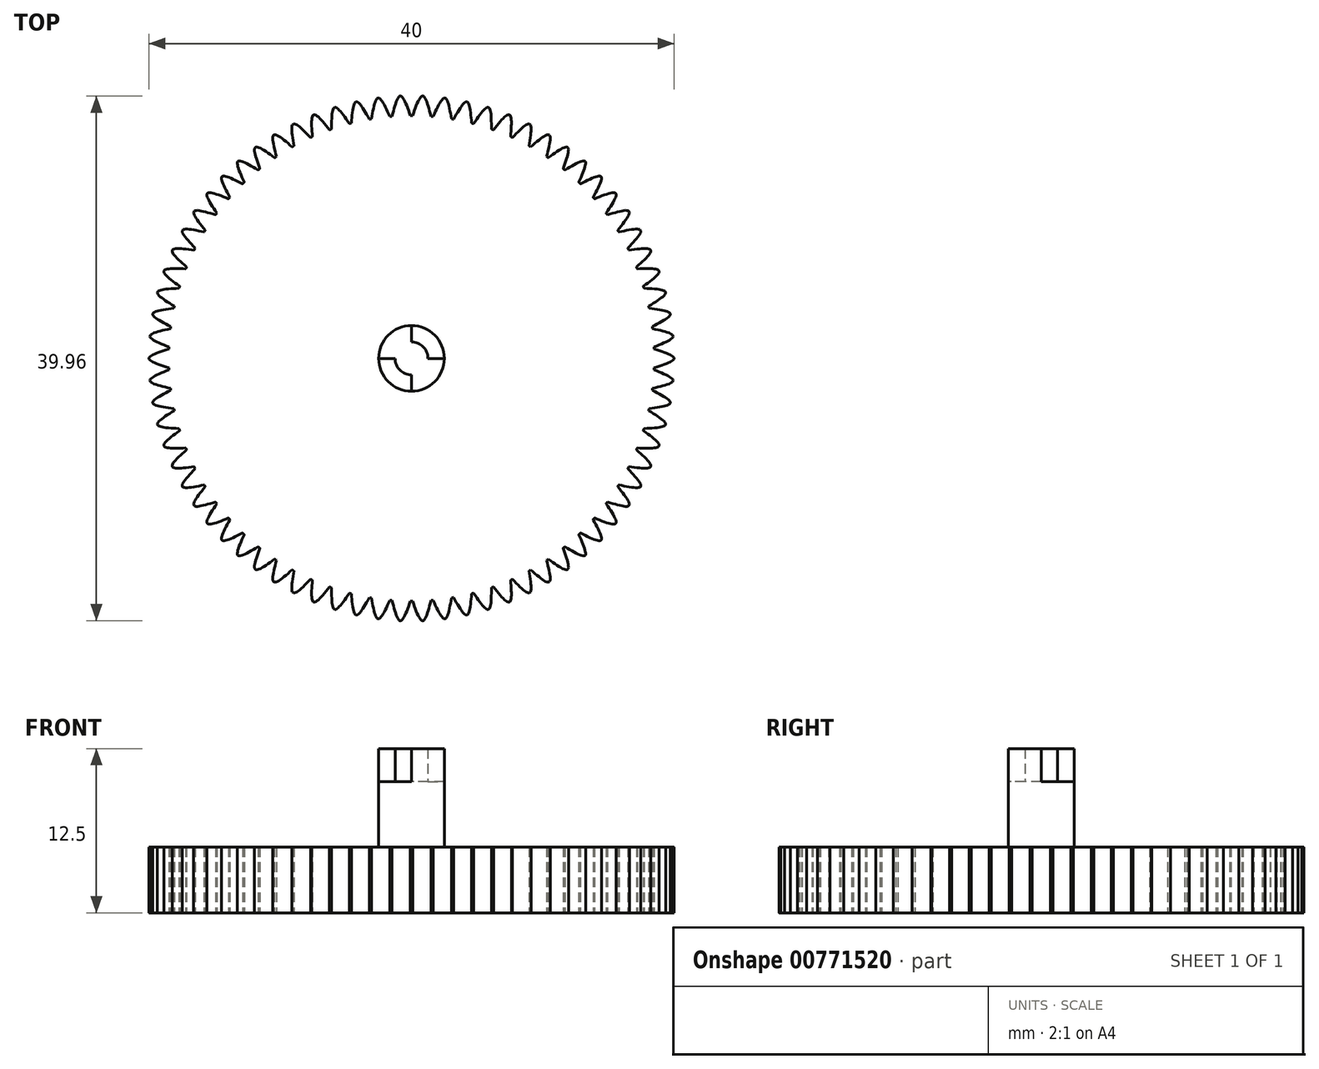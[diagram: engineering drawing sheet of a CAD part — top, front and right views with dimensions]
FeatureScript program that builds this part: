
annotation { "Feature Type Name" : "Feature", "Feature Type Description" : "" }
export const myFeature = defineFeature(function(context is Context, id is Id, definition is map)
    precondition{}
    {
        {
            var Q0;
            Q0=qCreatedBy(makeId("Top.planeOp"),FACE);
            var sketch = newSketch(context, id + "F0", { "sketchPlane" : qUnion([Q0])});
            skLineSegment(sketch, "E0", {"start": v(0, 0) * mm, "end": v(18.5, 0) * mm, "construction": true});
            skLineSegment(sketch, "E1", {"start": v(18.5, 0) * mm, "end": v(-20, 0) * mm, "construction": true});
            skCircle(sketch, "E2", {"center": v(0, 0) * mm, "radius": 18.5 * mm});
            skLineSegment(sketch, "E3", {"start": v(-18.5, 0) * mm, "end": v(-18.5, 0.7) * mm, "construction": true});
            skLineSegment(sketch, "E4", {"start": v(-18.5, 0.7) * mm, "end": v(-18.5, -0.7) * mm, "construction": true});
            skLineSegment(sketch, "E5", {"start": v(-18.5, -0.7) * mm, "end": v(-18.49, -0.7) * mm, "construction": true});
            skLineSegment(sketch, "E6", {"start": v(-18.49, -0.7) * mm, "end": v(-18.49, 0.7) * mm, "construction": true});
            skLineSegment(sketch, "E7", {"start": v(-18.49, 0.7) * mm, "end": v(-18.5, 0.7) * mm, "construction": true});
            skFitSpline(sketch, "E8", {"points": [v(-18.49, -0.7) * mm, v(-20, 0) * mm, v(-18.49, 0.7) * mm], "startDerivative": vector(-4.69, 1.4) * mm, "endDerivative": vector(4.69, 1.4) * mm});
            skSolve(sketch);
        }
        {
            var Q0;
            {var subQ0=sQuery(id+"F0.wireOp",EDGE,"E8");var subQ1=sQuery(id+"F0.wireOp",EDGE,"E2");var subQ2=makeQuery(id+"F0.imprint","INTERSECT",VERTEX,{"disambiguationData":[OD(0.0)],"derivedFrom":[subQ1,subQ0]});Q0=makeQuery(id+"F0.imprint","IMPRINT",FACE,{"disambiguationData":[TD([[makeQuery(id+"F0.imprint","IMPRINT",EDGE,{"disambiguationData":[TD([[subQ2,1.0]])],"derivedFrom":subQ1}),1.0]])]});}
            var Q1;
            {var subQ0=sQuery(id+"F0.wireOp",EDGE,"E8");Q1=makeQuery(id+"F0.imprint","IMPRINT",FACE,{"disambiguationData":[TD([[makeQuery(id+"F0.imprint","IMPRINT",EDGE,{"derivedFrom":subQ0}),-1.0]])]});}
            extrude(context, id + "F1", {"entities" : qUnion([Q0, Q1]), "depth" : 5 * mm, "offsetDistance" : 25 * mm});
        }
        {
            var Q0;
            Q0=makeQuery(id+"F1.opExtrude","SWEPT_BODY",BODY,{"disambiguationData":[OSD([sQuery(id+"F0.wireOp",EDGE,"E2"),sQuery(id+"F0.wireOp",EDGE,"E8")])]});
            var Q1;
            Q1=sQuery(id+"F0.wireOp",EDGE,"E2");
            circularPattern(context, id + "F2", {"entities" : qUnion([Q0]), "axis" : qUnion([Q1]), "angle" : 360 * degree, "instanceCount" : 74, "equalSpace" : true});
        }
        {
            var Q0;
            Q0=makeQuery(id+"F2.opPattern","COPY",BODY,{"derivedFrom":makeQuery(id+"F1.opExtrude","SWEPT_BODY",BODY,{"disambiguationData":[OSD([sQuery(id+"F0.wireOp",EDGE,"rMVjyNJe-mwVF-HOql-274t-2KQgdZwxYzZl"),sQuery(id+"F0.wireOp",EDGE,"E2"),sQuery(id+"F0.wireOp",EDGE,"E8")])]}),"instanceName":"10"});
            var Q1;
            Q1=makeQuery(id+"F2.opPattern","COPY",BODY,{"derivedFrom":makeQuery(id+"F1.opExtrude","SWEPT_BODY",BODY,{"disambiguationData":[OSD([sQuery(id+"F0.wireOp",EDGE,"rMVjyNJe-mwVF-HOql-274t-2KQgdZwxYzZl"),sQuery(id+"F0.wireOp",EDGE,"E2"),sQuery(id+"F0.wireOp",EDGE,"E8")])]}),"instanceName":"16"});
            var Q2;
            Q2=makeQuery(id+"F2.opPattern","COPY",BODY,{"derivedFrom":makeQuery(id+"F1.opExtrude","SWEPT_BODY",BODY,{"disambiguationData":[OSD([sQuery(id+"F0.wireOp",EDGE,"rMVjyNJe-mwVF-HOql-274t-2KQgdZwxYzZl"),sQuery(id+"F0.wireOp",EDGE,"E2"),sQuery(id+"F0.wireOp",EDGE,"E8")])]}),"instanceName":"15"});
            var Q3;
            Q3=makeQuery(id+"F2.opPattern","COPY",BODY,{"derivedFrom":makeQuery(id+"F1.opExtrude","SWEPT_BODY",BODY,{"disambiguationData":[OSD([sQuery(id+"F0.wireOp",EDGE,"rMVjyNJe-mwVF-HOql-274t-2KQgdZwxYzZl"),sQuery(id+"F0.wireOp",EDGE,"E2"),sQuery(id+"F0.wireOp",EDGE,"E8")])]}),"instanceName":"14"});
            var Q4;
            Q4=makeQuery(id+"F2.opPattern","COPY",BODY,{"derivedFrom":makeQuery(id+"F1.opExtrude","SWEPT_BODY",BODY,{"disambiguationData":[OSD([sQuery(id+"F0.wireOp",EDGE,"rMVjyNJe-mwVF-HOql-274t-2KQgdZwxYzZl"),sQuery(id+"F0.wireOp",EDGE,"E2"),sQuery(id+"F0.wireOp",EDGE,"E8")])]}),"instanceName":"13"});
            var Q5;
            Q5=makeQuery(id+"F2.opPattern","COPY",BODY,{"derivedFrom":makeQuery(id+"F1.opExtrude","SWEPT_BODY",BODY,{"disambiguationData":[OSD([sQuery(id+"F0.wireOp",EDGE,"rMVjyNJe-mwVF-HOql-274t-2KQgdZwxYzZl"),sQuery(id+"F0.wireOp",EDGE,"E2"),sQuery(id+"F0.wireOp",EDGE,"E8")])]}),"instanceName":"12"});
            var Q6;
            Q6=makeQuery(id+"F2.opPattern","COPY",BODY,{"derivedFrom":makeQuery(id+"F1.opExtrude","SWEPT_BODY",BODY,{"disambiguationData":[OSD([sQuery(id+"F0.wireOp",EDGE,"rMVjyNJe-mwVF-HOql-274t-2KQgdZwxYzZl"),sQuery(id+"F0.wireOp",EDGE,"E2"),sQuery(id+"F0.wireOp",EDGE,"E8")])]}),"instanceName":"11"});
            var Q7;
            Q7=makeQuery(id+"F2.opPattern","COPY",BODY,{"derivedFrom":makeQuery(id+"F1.opExtrude","SWEPT_BODY",BODY,{"disambiguationData":[OSD([sQuery(id+"F0.wireOp",EDGE,"rMVjyNJe-mwVF-HOql-274t-2KQgdZwxYzZl"),sQuery(id+"F0.wireOp",EDGE,"E2"),sQuery(id+"F0.wireOp",EDGE,"E8")])]}),"instanceName":"9"});
            var Q8;
            Q8=makeQuery(id+"F2.opPattern","COPY",BODY,{"derivedFrom":makeQuery(id+"F1.opExtrude","SWEPT_BODY",BODY,{"disambiguationData":[OSD([sQuery(id+"F0.wireOp",EDGE,"rMVjyNJe-mwVF-HOql-274t-2KQgdZwxYzZl"),sQuery(id+"F0.wireOp",EDGE,"E2"),sQuery(id+"F0.wireOp",EDGE,"E8")])]}),"instanceName":"7"});
            var Q9;
            Q9=makeQuery(id+"F2.opPattern","COPY",BODY,{"derivedFrom":makeQuery(id+"F1.opExtrude","SWEPT_BODY",BODY,{"disambiguationData":[OSD([sQuery(id+"F0.wireOp",EDGE,"rMVjyNJe-mwVF-HOql-274t-2KQgdZwxYzZl"),sQuery(id+"F0.wireOp",EDGE,"E2"),sQuery(id+"F0.wireOp",EDGE,"E8")])]}),"instanceName":"5"});
            var Q10;
            Q10=makeQuery(id+"F2.opPattern","COPY",BODY,{"derivedFrom":makeQuery(id+"F1.opExtrude","SWEPT_BODY",BODY,{"disambiguationData":[OSD([sQuery(id+"F0.wireOp",EDGE,"rMVjyNJe-mwVF-HOql-274t-2KQgdZwxYzZl"),sQuery(id+"F0.wireOp",EDGE,"E2"),sQuery(id+"F0.wireOp",EDGE,"E8")])]}),"instanceName":"6"});
            var Q11;
            Q11=makeQuery(id+"F2.opPattern","COPY",BODY,{"derivedFrom":makeQuery(id+"F1.opExtrude","SWEPT_BODY",BODY,{"disambiguationData":[OSD([sQuery(id+"F0.wireOp",EDGE,"rMVjyNJe-mwVF-HOql-274t-2KQgdZwxYzZl"),sQuery(id+"F0.wireOp",EDGE,"E2"),sQuery(id+"F0.wireOp",EDGE,"E8")])]}),"instanceName":"4"});
            var Q12;
            Q12=makeQuery(id+"F2.opPattern","COPY",BODY,{"derivedFrom":makeQuery(id+"F1.opExtrude","SWEPT_BODY",BODY,{"disambiguationData":[OSD([sQuery(id+"F0.wireOp",EDGE,"rMVjyNJe-mwVF-HOql-274t-2KQgdZwxYzZl"),sQuery(id+"F0.wireOp",EDGE,"E2"),sQuery(id+"F0.wireOp",EDGE,"E8")])]}),"instanceName":"3"});
            var Q13;
            Q13=makeQuery(id+"F2.opPattern","COPY",BODY,{"derivedFrom":makeQuery(id+"F1.opExtrude","SWEPT_BODY",BODY,{"disambiguationData":[OSD([sQuery(id+"F0.wireOp",EDGE,"rMVjyNJe-mwVF-HOql-274t-2KQgdZwxYzZl"),sQuery(id+"F0.wireOp",EDGE,"E2"),sQuery(id+"F0.wireOp",EDGE,"E8")])]}),"instanceName":"2"});
            var Q14;
            Q14=makeQuery(id+"F1.opExtrude","SWEPT_BODY",BODY,{"disambiguationData":[OSD([sQuery(id+"F0.wireOp",EDGE,"rMVjyNJe-mwVF-HOql-274t-2KQgdZwxYzZl"),sQuery(id+"F0.wireOp",EDGE,"E2"),sQuery(id+"F0.wireOp",EDGE,"E8")])]});
            var Q15;
            Q15=makeQuery(id+"F2.opPattern","COPY",BODY,{"derivedFrom":makeQuery(id+"F1.opExtrude","SWEPT_BODY",BODY,{"disambiguationData":[OSD([sQuery(id+"F0.wireOp",EDGE,"rMVjyNJe-mwVF-HOql-274t-2KQgdZwxYzZl"),sQuery(id+"F0.wireOp",EDGE,"E2"),sQuery(id+"F0.wireOp",EDGE,"E8")])]}),"instanceName":"1"});
            var Q16;
            Q16=makeQuery(id+"F2.opPattern","COPY",BODY,{"derivedFrom":makeQuery(id+"F1.opExtrude","SWEPT_BODY",BODY,{"disambiguationData":[OSD([sQuery(id+"F0.wireOp",EDGE,"E2"),sQuery(id+"F0.wireOp",EDGE,"E8")])]}),"instanceName":"18"});
            var Q17;
            Q17=makeQuery(id+"F2.opPattern","COPY",BODY,{"derivedFrom":makeQuery(id+"F1.opExtrude","SWEPT_BODY",BODY,{"disambiguationData":[OSD([sQuery(id+"F0.wireOp",EDGE,"E2"),sQuery(id+"F0.wireOp",EDGE,"E8")])]}),"instanceName":"17"});
            var Q18;
            Q18=makeQuery(id+"F2.opPattern","COPY",BODY,{"derivedFrom":makeQuery(id+"F1.opExtrude","SWEPT_BODY",BODY,{"disambiguationData":[OSD([sQuery(id+"F0.wireOp",EDGE,"E2"),sQuery(id+"F0.wireOp",EDGE,"E8")])]}),"instanceName":"23"});
            var Q19;
            Q19=makeQuery(id+"F2.opPattern","COPY",BODY,{"derivedFrom":makeQuery(id+"F1.opExtrude","SWEPT_BODY",BODY,{"disambiguationData":[OSD([sQuery(id+"F0.wireOp",EDGE,"E2"),sQuery(id+"F0.wireOp",EDGE,"E8")])]}),"instanceName":"22"});
            var Q20;
            Q20=makeQuery(id+"F2.opPattern","COPY",BODY,{"derivedFrom":makeQuery(id+"F1.opExtrude","SWEPT_BODY",BODY,{"disambiguationData":[OSD([sQuery(id+"F0.wireOp",EDGE,"E2"),sQuery(id+"F0.wireOp",EDGE,"E8")])]}),"instanceName":"20"});
            var Q21;
            Q21=makeQuery(id+"F2.opPattern","COPY",BODY,{"derivedFrom":makeQuery(id+"F1.opExtrude","SWEPT_BODY",BODY,{"disambiguationData":[OSD([sQuery(id+"F0.wireOp",EDGE,"E2"),sQuery(id+"F0.wireOp",EDGE,"E8")])]}),"instanceName":"19"});
            var Q22;
            Q22=makeQuery(id+"F2.opPattern","COPY",BODY,{"derivedFrom":makeQuery(id+"F1.opExtrude","SWEPT_BODY",BODY,{"disambiguationData":[OSD([sQuery(id+"F0.wireOp",EDGE,"E2"),sQuery(id+"F0.wireOp",EDGE,"E8")])]}),"instanceName":"21"});
            var Q23;
            Q23=makeQuery(id+"F2.opPattern","COPY",BODY,{"derivedFrom":makeQuery(id+"F1.opExtrude","SWEPT_BODY",BODY,{"disambiguationData":[OSD([sQuery(id+"F0.wireOp",EDGE,"E2"),sQuery(id+"F0.wireOp",EDGE,"E8")])]}),"instanceName":"31"});
            var Q24;
            Q24=makeQuery(id+"F2.opPattern","COPY",BODY,{"derivedFrom":makeQuery(id+"F1.opExtrude","SWEPT_BODY",BODY,{"disambiguationData":[OSD([sQuery(id+"F0.wireOp",EDGE,"E2"),sQuery(id+"F0.wireOp",EDGE,"E8")])]}),"instanceName":"30"});
            var Q25;
            Q25=makeQuery(id+"F2.opPattern","COPY",BODY,{"derivedFrom":makeQuery(id+"F1.opExtrude","SWEPT_BODY",BODY,{"disambiguationData":[OSD([sQuery(id+"F0.wireOp",EDGE,"E2"),sQuery(id+"F0.wireOp",EDGE,"E8")])]}),"instanceName":"28"});
            var Q26;
            Q26=makeQuery(id+"F2.opPattern","COPY",BODY,{"derivedFrom":makeQuery(id+"F1.opExtrude","SWEPT_BODY",BODY,{"disambiguationData":[OSD([sQuery(id+"F0.wireOp",EDGE,"E2"),sQuery(id+"F0.wireOp",EDGE,"E8")])]}),"instanceName":"29"});
            var Q27;
            Q27=makeQuery(id+"F2.opPattern","COPY",BODY,{"derivedFrom":makeQuery(id+"F1.opExtrude","SWEPT_BODY",BODY,{"disambiguationData":[OSD([sQuery(id+"F0.wireOp",EDGE,"E2"),sQuery(id+"F0.wireOp",EDGE,"E8")])]}),"instanceName":"27"});
            var Q28;
            Q28=makeQuery(id+"F2.opPattern","COPY",BODY,{"derivedFrom":makeQuery(id+"F1.opExtrude","SWEPT_BODY",BODY,{"disambiguationData":[OSD([sQuery(id+"F0.wireOp",EDGE,"E2"),sQuery(id+"F0.wireOp",EDGE,"E8")])]}),"instanceName":"24"});
            var Q29;
            Q29=makeQuery(id+"F2.opPattern","COPY",BODY,{"derivedFrom":makeQuery(id+"F1.opExtrude","SWEPT_BODY",BODY,{"disambiguationData":[OSD([sQuery(id+"F0.wireOp",EDGE,"E2"),sQuery(id+"F0.wireOp",EDGE,"E8")])]}),"instanceName":"25"});
            var Q30;
            Q30=makeQuery(id+"F2.opPattern","COPY",BODY,{"derivedFrom":makeQuery(id+"F1.opExtrude","SWEPT_BODY",BODY,{"disambiguationData":[OSD([sQuery(id+"F0.wireOp",EDGE,"E2"),sQuery(id+"F0.wireOp",EDGE,"E8")])]}),"instanceName":"26"});
            var Q31;
            Q31=makeQuery(id+"F2.opPattern","COPY",BODY,{"derivedFrom":makeQuery(id+"F1.opExtrude","SWEPT_BODY",BODY,{"disambiguationData":[OSD([sQuery(id+"F0.wireOp",EDGE,"E2"),sQuery(id+"F0.wireOp",EDGE,"E8")])]}),"instanceName":"33"});
            var Q32;
            Q32=makeQuery(id+"F2.opPattern","COPY",BODY,{"derivedFrom":makeQuery(id+"F1.opExtrude","SWEPT_BODY",BODY,{"disambiguationData":[OSD([sQuery(id+"F0.wireOp",EDGE,"E2"),sQuery(id+"F0.wireOp",EDGE,"E8")])]}),"instanceName":"34"});
            var Q33;
            Q33=makeQuery(id+"F2.opPattern","COPY",BODY,{"derivedFrom":makeQuery(id+"F1.opExtrude","SWEPT_BODY",BODY,{"disambiguationData":[OSD([sQuery(id+"F0.wireOp",EDGE,"E2"),sQuery(id+"F0.wireOp",EDGE,"E8")])]}),"instanceName":"35"});
            var Q34;
            Q34=makeQuery(id+"F2.opPattern","COPY",BODY,{"derivedFrom":makeQuery(id+"F1.opExtrude","SWEPT_BODY",BODY,{"disambiguationData":[OSD([sQuery(id+"F0.wireOp",EDGE,"E2"),sQuery(id+"F0.wireOp",EDGE,"E8")])]}),"instanceName":"36"});
            var Q35;
            Q35=makeQuery(id+"F2.opPattern","COPY",BODY,{"derivedFrom":makeQuery(id+"F1.opExtrude","SWEPT_BODY",BODY,{"disambiguationData":[OSD([sQuery(id+"F0.wireOp",EDGE,"E2"),sQuery(id+"F0.wireOp",EDGE,"E8")])]}),"instanceName":"32"});
            var Q36;
            Q36=makeQuery(id+"F2.opPattern","COPY",BODY,{"derivedFrom":makeQuery(id+"F1.opExtrude","SWEPT_BODY",BODY,{"disambiguationData":[OSD([sQuery(id+"F0.wireOp",EDGE,"E2"),sQuery(id+"F0.wireOp",EDGE,"E8")])]}),"instanceName":"32"});
            var Q37;
            Q37=makeQuery(id+"F2.opPattern","COPY",BODY,{"derivedFrom":makeQuery(id+"F1.opExtrude","SWEPT_BODY",BODY,{"disambiguationData":[OSD([sQuery(id+"F0.wireOp",EDGE,"E2"),sQuery(id+"F0.wireOp",EDGE,"E8")])]}),"instanceName":"37"});
            var Q38;
            Q38=makeQuery(id+"F2.opPattern","COPY",BODY,{"derivedFrom":makeQuery(id+"F1.opExtrude","SWEPT_BODY",BODY,{"disambiguationData":[OSD([sQuery(id+"F0.wireOp",EDGE,"E2"),sQuery(id+"F0.wireOp",EDGE,"E8")])]}),"instanceName":"38"});
            var Q39;
            Q39=makeQuery(id+"F2.opPattern","COPY",BODY,{"derivedFrom":makeQuery(id+"F1.opExtrude","SWEPT_BODY",BODY,{"disambiguationData":[OSD([sQuery(id+"F0.wireOp",EDGE,"E2"),sQuery(id+"F0.wireOp",EDGE,"E8")])]}),"instanceName":"39"});
            var Q40;
            Q40=makeQuery(id+"F2.opPattern","COPY",BODY,{"derivedFrom":makeQuery(id+"F1.opExtrude","SWEPT_BODY",BODY,{"disambiguationData":[OSD([sQuery(id+"F0.wireOp",EDGE,"E2"),sQuery(id+"F0.wireOp",EDGE,"E8")])]}),"instanceName":"40"});
            var Q41;
            Q41=makeQuery(id+"F2.opPattern","COPY",BODY,{"derivedFrom":makeQuery(id+"F1.opExtrude","SWEPT_BODY",BODY,{"disambiguationData":[OSD([sQuery(id+"F0.wireOp",EDGE,"E2"),sQuery(id+"F0.wireOp",EDGE,"E8")])]}),"instanceName":"42"});
            var Q42;
            Q42=makeQuery(id+"F2.opPattern","COPY",BODY,{"derivedFrom":makeQuery(id+"F1.opExtrude","SWEPT_BODY",BODY,{"disambiguationData":[OSD([sQuery(id+"F0.wireOp",EDGE,"E2"),sQuery(id+"F0.wireOp",EDGE,"E8")])]}),"instanceName":"43"});
            var Q43;
            Q43=makeQuery(id+"F2.opPattern","COPY",BODY,{"derivedFrom":makeQuery(id+"F1.opExtrude","SWEPT_BODY",BODY,{"disambiguationData":[OSD([sQuery(id+"F0.wireOp",EDGE,"E2"),sQuery(id+"F0.wireOp",EDGE,"E8")])]}),"instanceName":"44"});
            var Q44;
            Q44=makeQuery(id+"F2.opPattern","COPY",BODY,{"derivedFrom":makeQuery(id+"F1.opExtrude","SWEPT_BODY",BODY,{"disambiguationData":[OSD([sQuery(id+"F0.wireOp",EDGE,"E2"),sQuery(id+"F0.wireOp",EDGE,"E8")])]}),"instanceName":"46"});
            var Q45;
            Q45=makeQuery(id+"F2.opPattern","COPY",BODY,{"derivedFrom":makeQuery(id+"F1.opExtrude","SWEPT_BODY",BODY,{"disambiguationData":[OSD([sQuery(id+"F0.wireOp",EDGE,"E2"),sQuery(id+"F0.wireOp",EDGE,"E8")])]}),"instanceName":"45"});
            var Q46;
            Q46=makeQuery(id+"F2.opPattern","COPY",BODY,{"derivedFrom":makeQuery(id+"F1.opExtrude","SWEPT_BODY",BODY,{"disambiguationData":[OSD([sQuery(id+"F0.wireOp",EDGE,"E2"),sQuery(id+"F0.wireOp",EDGE,"E8")])]}),"instanceName":"47"});
            var Q47;
            Q47=makeQuery(id+"F2.opPattern","COPY",BODY,{"derivedFrom":makeQuery(id+"F1.opExtrude","SWEPT_BODY",BODY,{"disambiguationData":[OSD([sQuery(id+"F0.wireOp",EDGE,"E2"),sQuery(id+"F0.wireOp",EDGE,"E8")])]}),"instanceName":"48"});
            var Q48;
            Q48=makeQuery(id+"F2.opPattern","COPY",BODY,{"derivedFrom":makeQuery(id+"F1.opExtrude","SWEPT_BODY",BODY,{"disambiguationData":[OSD([sQuery(id+"F0.wireOp",EDGE,"E2"),sQuery(id+"F0.wireOp",EDGE,"E8")])]}),"instanceName":"49"});
            var Q49;
            Q49=makeQuery(id+"F2.opPattern","COPY",BODY,{"derivedFrom":makeQuery(id+"F1.opExtrude","SWEPT_BODY",BODY,{"disambiguationData":[OSD([sQuery(id+"F0.wireOp",EDGE,"E2"),sQuery(id+"F0.wireOp",EDGE,"E8")])]}),"instanceName":"50"});
            var Q50;
            Q50=makeQuery(id+"F2.opPattern","COPY",BODY,{"derivedFrom":makeQuery(id+"F1.opExtrude","SWEPT_BODY",BODY,{"disambiguationData":[OSD([sQuery(id+"F0.wireOp",EDGE,"E2"),sQuery(id+"F0.wireOp",EDGE,"E8")])]}),"instanceName":"41"});
            var Q51;
            Q51=makeQuery(id+"F2.opPattern","COPY",BODY,{"derivedFrom":makeQuery(id+"F1.opExtrude","SWEPT_BODY",BODY,{"disambiguationData":[OSD([sQuery(id+"F0.wireOp",EDGE,"E2"),sQuery(id+"F0.wireOp",EDGE,"E8")])]}),"instanceName":"51"});
            var Q52;
            Q52=makeQuery(id+"F2.opPattern","COPY",BODY,{"derivedFrom":makeQuery(id+"F1.opExtrude","SWEPT_BODY",BODY,{"disambiguationData":[OSD([sQuery(id+"F0.wireOp",EDGE,"E2"),sQuery(id+"F0.wireOp",EDGE,"E8")])]}),"instanceName":"52"});
            var Q53;
            Q53=makeQuery(id+"F2.opPattern","COPY",BODY,{"derivedFrom":makeQuery(id+"F1.opExtrude","SWEPT_BODY",BODY,{"disambiguationData":[OSD([sQuery(id+"F0.wireOp",EDGE,"E2"),sQuery(id+"F0.wireOp",EDGE,"E8")])]}),"instanceName":"53"});
            var Q54;
            Q54=makeQuery(id+"F2.opPattern","COPY",BODY,{"derivedFrom":makeQuery(id+"F1.opExtrude","SWEPT_BODY",BODY,{"disambiguationData":[OSD([sQuery(id+"F0.wireOp",EDGE,"E2"),sQuery(id+"F0.wireOp",EDGE,"E8")])]}),"instanceName":"54"});
            var Q55;
            Q55=makeQuery(id+"F2.opPattern","COPY",BODY,{"derivedFrom":makeQuery(id+"F1.opExtrude","SWEPT_BODY",BODY,{"disambiguationData":[OSD([sQuery(id+"F0.wireOp",EDGE,"E2"),sQuery(id+"F0.wireOp",EDGE,"E8")])]}),"instanceName":"56"});
            var Q56;
            Q56=makeQuery(id+"F2.opPattern","COPY",BODY,{"derivedFrom":makeQuery(id+"F1.opExtrude","SWEPT_BODY",BODY,{"disambiguationData":[OSD([sQuery(id+"F0.wireOp",EDGE,"E2"),sQuery(id+"F0.wireOp",EDGE,"E8")])]}),"instanceName":"57"});
            var Q57;
            Q57=makeQuery(id+"F2.opPattern","COPY",BODY,{"derivedFrom":makeQuery(id+"F1.opExtrude","SWEPT_BODY",BODY,{"disambiguationData":[OSD([sQuery(id+"F0.wireOp",EDGE,"E2"),sQuery(id+"F0.wireOp",EDGE,"E8")])]}),"instanceName":"58"});
            var Q58;
            Q58=makeQuery(id+"F2.opPattern","COPY",BODY,{"derivedFrom":makeQuery(id+"F1.opExtrude","SWEPT_BODY",BODY,{"disambiguationData":[OSD([sQuery(id+"F0.wireOp",EDGE,"E2"),sQuery(id+"F0.wireOp",EDGE,"E8")])]}),"instanceName":"59"});
            var Q59;
            Q59=makeQuery(id+"F2.opPattern","COPY",BODY,{"derivedFrom":makeQuery(id+"F1.opExtrude","SWEPT_BODY",BODY,{"disambiguationData":[OSD([sQuery(id+"F0.wireOp",EDGE,"E2"),sQuery(id+"F0.wireOp",EDGE,"E8")])]}),"instanceName":"60"});
            var Q60;
            Q60=makeQuery(id+"F2.opPattern","COPY",BODY,{"derivedFrom":makeQuery(id+"F1.opExtrude","SWEPT_BODY",BODY,{"disambiguationData":[OSD([sQuery(id+"F0.wireOp",EDGE,"E2"),sQuery(id+"F0.wireOp",EDGE,"E8")])]}),"instanceName":"62"});
            var Q61;
            Q61=makeQuery(id+"F2.opPattern","COPY",BODY,{"derivedFrom":makeQuery(id+"F1.opExtrude","SWEPT_BODY",BODY,{"disambiguationData":[OSD([sQuery(id+"F0.wireOp",EDGE,"E2"),sQuery(id+"F0.wireOp",EDGE,"E8")])]}),"instanceName":"61"});
            var Q62;
            Q62=makeQuery(id+"F2.opPattern","COPY",BODY,{"derivedFrom":makeQuery(id+"F1.opExtrude","SWEPT_BODY",BODY,{"disambiguationData":[OSD([sQuery(id+"F0.wireOp",EDGE,"E2"),sQuery(id+"F0.wireOp",EDGE,"E8")])]}),"instanceName":"63"});
            var Q63;
            Q63=makeQuery(id+"F2.opPattern","COPY",BODY,{"derivedFrom":makeQuery(id+"F1.opExtrude","SWEPT_BODY",BODY,{"disambiguationData":[OSD([sQuery(id+"F0.wireOp",EDGE,"E2"),sQuery(id+"F0.wireOp",EDGE,"E8")])]}),"instanceName":"55"});
            var Q64;
            Q64=makeQuery(id+"F2.opPattern","COPY",BODY,{"derivedFrom":makeQuery(id+"F1.opExtrude","SWEPT_BODY",BODY,{"disambiguationData":[OSD([sQuery(id+"F0.wireOp",EDGE,"E2"),sQuery(id+"F0.wireOp",EDGE,"E8")])]}),"instanceName":"64"});
            var Q65;
            Q65=makeQuery(id+"F2.opPattern","COPY",BODY,{"derivedFrom":makeQuery(id+"F1.opExtrude","SWEPT_BODY",BODY,{"disambiguationData":[OSD([sQuery(id+"F0.wireOp",EDGE,"E2"),sQuery(id+"F0.wireOp",EDGE,"E8")])]}),"instanceName":"65"});
            var Q66;
            Q66=makeQuery(id+"F2.opPattern","COPY",BODY,{"derivedFrom":makeQuery(id+"F1.opExtrude","SWEPT_BODY",BODY,{"disambiguationData":[OSD([sQuery(id+"F0.wireOp",EDGE,"E2"),sQuery(id+"F0.wireOp",EDGE,"E8")])]}),"instanceName":"66"});
            var Q67;
            Q67=makeQuery(id+"F2.opPattern","COPY",BODY,{"derivedFrom":makeQuery(id+"F1.opExtrude","SWEPT_BODY",BODY,{"disambiguationData":[OSD([sQuery(id+"F0.wireOp",EDGE,"E2"),sQuery(id+"F0.wireOp",EDGE,"E8")])]}),"instanceName":"67"});
            var Q68;
            Q68=makeQuery(id+"F2.opPattern","COPY",BODY,{"derivedFrom":makeQuery(id+"F1.opExtrude","SWEPT_BODY",BODY,{"disambiguationData":[OSD([sQuery(id+"F0.wireOp",EDGE,"E2"),sQuery(id+"F0.wireOp",EDGE,"E8")])]}),"instanceName":"68"});
            var Q69;
            Q69=makeQuery(id+"F2.opPattern","COPY",BODY,{"derivedFrom":makeQuery(id+"F1.opExtrude","SWEPT_BODY",BODY,{"disambiguationData":[OSD([sQuery(id+"F0.wireOp",EDGE,"E2"),sQuery(id+"F0.wireOp",EDGE,"E8")])]}),"instanceName":"69"});
            var Q70;
            Q70=makeQuery(id+"F2.opPattern","COPY",BODY,{"derivedFrom":makeQuery(id+"F1.opExtrude","SWEPT_BODY",BODY,{"disambiguationData":[OSD([sQuery(id+"F0.wireOp",EDGE,"E2"),sQuery(id+"F0.wireOp",EDGE,"E8")])]}),"instanceName":"70"});
            var Q71;
            Q71=makeQuery(id+"F2.opPattern","COPY",BODY,{"derivedFrom":makeQuery(id+"F1.opExtrude","SWEPT_BODY",BODY,{"disambiguationData":[OSD([sQuery(id+"F0.wireOp",EDGE,"E2"),sQuery(id+"F0.wireOp",EDGE,"E8")])]}),"instanceName":"71"});
            var Q72;
            Q72=makeQuery(id+"F2.opPattern","COPY",BODY,{"derivedFrom":makeQuery(id+"F1.opExtrude","SWEPT_BODY",BODY,{"disambiguationData":[OSD([sQuery(id+"F0.wireOp",EDGE,"E2"),sQuery(id+"F0.wireOp",EDGE,"E8")])]}),"instanceName":"72"});
            var Q73;
            Q73=makeQuery(id+"F2.opPattern","COPY",BODY,{"derivedFrom":makeQuery(id+"F1.opExtrude","SWEPT_BODY",BODY,{"disambiguationData":[OSD([sQuery(id+"F0.wireOp",EDGE,"E2"),sQuery(id+"F0.wireOp",EDGE,"E8")])]}),"instanceName":"73"});
            var Q74;
            Q74=makeQuery(id+"F2.opPattern","COPY",BODY,{"derivedFrom":makeQuery(id+"F1.opExtrude","SWEPT_BODY",BODY,{"disambiguationData":[OSD([sQuery(id+"F0.wireOp",EDGE,"E2"),sQuery(id+"F0.wireOp",EDGE,"E8")])]}),"instanceName":"68"});
            var Q75;
            Q75=makeQuery(id+"F2.opPattern","COPY",BODY,{"derivedFrom":makeQuery(id+"F1.opExtrude","SWEPT_BODY",BODY,{"disambiguationData":[OSD([sQuery(id+"F0.wireOp",EDGE,"E2"),sQuery(id+"F0.wireOp",EDGE,"E8")])]}),"instanceName":"69"});
            var Q76;
            Q76=makeQuery(id+"F2.opPattern","COPY",BODY,{"derivedFrom":makeQuery(id+"F1.opExtrude","SWEPT_BODY",BODY,{"disambiguationData":[OSD([sQuery(id+"F0.wireOp",EDGE,"E2"),sQuery(id+"F0.wireOp",EDGE,"E8")])]}),"instanceName":"70"});
            var Q77;
            Q77=makeQuery(id+"F2.opPattern","COPY",BODY,{"derivedFrom":makeQuery(id+"F1.opExtrude","SWEPT_BODY",BODY,{"disambiguationData":[OSD([sQuery(id+"F0.wireOp",EDGE,"E2"),sQuery(id+"F0.wireOp",EDGE,"E8")])]}),"instanceName":"71"});
            var Q78;
            Q78=makeQuery(id+"F2.opPattern","COPY",BODY,{"derivedFrom":makeQuery(id+"F1.opExtrude","SWEPT_BODY",BODY,{"disambiguationData":[OSD([sQuery(id+"F0.wireOp",EDGE,"E2"),sQuery(id+"F0.wireOp",EDGE,"E8")])]}),"instanceName":"72"});
            var Q79;
            Q79=makeQuery(id+"F2.opPattern","COPY",BODY,{"derivedFrom":makeQuery(id+"F1.opExtrude","SWEPT_BODY",BODY,{"disambiguationData":[OSD([sQuery(id+"F0.wireOp",EDGE,"E2"),sQuery(id+"F0.wireOp",EDGE,"E8")])]}),"instanceName":"73"});
            var Q80;
            Q80=makeQuery(id+"F2.opPattern","COPY",BODY,{"derivedFrom":makeQuery(id+"F1.opExtrude","SWEPT_BODY",BODY,{"disambiguationData":[OSD([sQuery(id+"F0.wireOp",EDGE,"E2"),sQuery(id+"F0.wireOp",EDGE,"E8")])]}),"instanceName":"66"});
            var Q81;
            Q81=makeQuery(id+"F2.opPattern","COPY",BODY,{"derivedFrom":makeQuery(id+"F1.opExtrude","SWEPT_BODY",BODY,{"disambiguationData":[OSD([sQuery(id+"F0.wireOp",EDGE,"E2"),sQuery(id+"F0.wireOp",EDGE,"E8")])]}),"instanceName":"67"});
            var Q82;
            Q82=makeQuery(id+"F2.opPattern","COPY",BODY,{"derivedFrom":makeQuery(id+"F1.opExtrude","SWEPT_BODY",BODY,{"disambiguationData":[OSD([sQuery(id+"F0.wireOp",EDGE,"E2"),sQuery(id+"F0.wireOp",EDGE,"E8")])]}),"instanceName":"64"});
            var Q83;
            Q83=makeQuery(id+"F2.opPattern","COPY",BODY,{"derivedFrom":makeQuery(id+"F1.opExtrude","SWEPT_BODY",BODY,{"disambiguationData":[OSD([sQuery(id+"F0.wireOp",EDGE,"E2"),sQuery(id+"F0.wireOp",EDGE,"E8")])]}),"instanceName":"8"});
            var Q84;
            Q84=makeQuery(id+"F2.opPattern","COPY",BODY,{"derivedFrom":makeQuery(id+"F1.opExtrude","SWEPT_BODY",BODY,{"disambiguationData":[OSD([sQuery(id+"F0.wireOp",EDGE,"E2"),sQuery(id+"F0.wireOp",EDGE,"E8")])]}),"instanceName":"65"});
            booleanBodies(context, id + "F3", {"operationType" : BooleanOperationType.UNION, "tools" : qUnion([Q0, Q1, Q2, Q3, Q4, Q5, Q6, Q7, Q8, Q9, Q10, Q11, Q12, Q13, Q14, Q15, Q16, Q17, Q18, Q19, Q20, Q21, Q22, Q23, Q24, Q25, Q26, Q27, Q28, Q29, Q30, Q31, Q32, Q33, Q34, Q35, Q36, Q37, Q38, Q39, Q40, Q41, Q42, Q43, Q44, Q45, Q46, Q47, Q48, Q49, Q50, Q51, Q52, Q53, Q54, Q55, Q56, Q57, Q58, Q59, Q60, Q61, Q62, Q63, Q64, Q65, Q66, Q67, Q68, Q69, Q70, Q71, Q72, Q73, Q74, Q75, Q76, Q77, Q78, Q79, Q80, Q81, Q82, Q83, Q84])});
        }
        {
            var Q0;
            {var subQ0=makeQuery(id+"F1.opExtrude","CAP_FACE",FACE,{"disambiguationData":[OSD([sQuery(id+"F0.wireOp",EDGE,"E2"),sQuery(id+"F0.wireOp",EDGE,"E8")])],"isStart":false});Q0=makeQuery(id+"F3.opBoolean","MERGE",FACE,{"derivedFrom":[subQ0,makeQuery(id+"F2.opPattern","COPY",FACE,{"derivedFrom":subQ0,"instanceName":"1"}),makeQuery(id+"F2.opPattern","COPY",FACE,{"derivedFrom":subQ0,"instanceName":"2"}),makeQuery(id+"F2.opPattern","COPY",FACE,{"derivedFrom":subQ0,"instanceName":"3"}),makeQuery(id+"F2.opPattern","COPY",FACE,{"derivedFrom":subQ0,"instanceName":"4"}),makeQuery(id+"F2.opPattern","COPY",FACE,{"derivedFrom":subQ0,"instanceName":"5"}),makeQuery(id+"F2.opPattern","COPY",FACE,{"derivedFrom":subQ0,"instanceName":"6"}),makeQuery(id+"F2.opPattern","COPY",FACE,{"derivedFrom":subQ0,"instanceName":"7"}),makeQuery(id+"F2.opPattern","COPY",FACE,{"derivedFrom":subQ0,"instanceName":"8"}),makeQuery(id+"F2.opPattern","COPY",FACE,{"derivedFrom":subQ0,"instanceName":"9"}),makeQuery(id+"F2.opPattern","COPY",FACE,{"derivedFrom":subQ0,"instanceName":"10"}),makeQuery(id+"F2.opPattern","COPY",FACE,{"derivedFrom":subQ0,"instanceName":"11"}),makeQuery(id+"F2.opPattern","COPY",FACE,{"derivedFrom":subQ0,"instanceName":"12"}),makeQuery(id+"F2.opPattern","COPY",FACE,{"derivedFrom":subQ0,"instanceName":"13"}),makeQuery(id+"F2.opPattern","COPY",FACE,{"derivedFrom":subQ0,"instanceName":"14"}),makeQuery(id+"F2.opPattern","COPY",FACE,{"derivedFrom":subQ0,"instanceName":"15"}),makeQuery(id+"F2.opPattern","COPY",FACE,{"derivedFrom":subQ0,"instanceName":"16"}),makeQuery(id+"F2.opPattern","COPY",FACE,{"derivedFrom":subQ0,"instanceName":"17"}),makeQuery(id+"F2.opPattern","COPY",FACE,{"derivedFrom":subQ0,"instanceName":"18"}),makeQuery(id+"F2.opPattern","COPY",FACE,{"derivedFrom":subQ0,"instanceName":"19"}),makeQuery(id+"F2.opPattern","COPY",FACE,{"derivedFrom":subQ0,"instanceName":"20"}),makeQuery(id+"F2.opPattern","COPY",FACE,{"derivedFrom":subQ0,"instanceName":"21"}),makeQuery(id+"F2.opPattern","COPY",FACE,{"derivedFrom":subQ0,"instanceName":"22"}),makeQuery(id+"F2.opPattern","COPY",FACE,{"derivedFrom":subQ0,"instanceName":"23"}),makeQuery(id+"F2.opPattern","COPY",FACE,{"derivedFrom":subQ0,"instanceName":"24"}),makeQuery(id+"F2.opPattern","COPY",FACE,{"derivedFrom":subQ0,"instanceName":"25"}),makeQuery(id+"F2.opPattern","COPY",FACE,{"derivedFrom":subQ0,"instanceName":"26"}),makeQuery(id+"F2.opPattern","COPY",FACE,{"derivedFrom":subQ0,"instanceName":"27"}),makeQuery(id+"F2.opPattern","COPY",FACE,{"derivedFrom":subQ0,"instanceName":"28"}),makeQuery(id+"F2.opPattern","COPY",FACE,{"derivedFrom":subQ0,"instanceName":"29"}),makeQuery(id+"F2.opPattern","COPY",FACE,{"derivedFrom":subQ0,"instanceName":"30"}),makeQuery(id+"F2.opPattern","COPY",FACE,{"derivedFrom":subQ0,"instanceName":"31"}),makeQuery(id+"F2.opPattern","COPY",FACE,{"derivedFrom":subQ0,"instanceName":"32"}),makeQuery(id+"F2.opPattern","COPY",FACE,{"derivedFrom":subQ0,"instanceName":"33"}),makeQuery(id+"F2.opPattern","COPY",FACE,{"derivedFrom":subQ0,"instanceName":"34"}),makeQuery(id+"F2.opPattern","COPY",FACE,{"derivedFrom":subQ0,"instanceName":"35"}),makeQuery(id+"F2.opPattern","COPY",FACE,{"derivedFrom":subQ0,"instanceName":"36"})]});}
            var sketch = newSketch(context, id + "F4", { "sketchPlane" : qUnion([Q0])});
            skCircle(sketch, "E9", {"center": v(0, 0) * mm, "radius": 2.5 * mm});
            skLineSegment(sketch, "E10", {"start": v(-2.5, 0) * mm, "end": v(2.5, 0) * mm});
            skLineSegment(sketch, "E11", {"start": v(0, 2.5) * mm, "end": v(0, -2.5) * mm});
            skCircle(sketch, "E12", {"center": v(0, 0) * mm, "radius": 1.25 * mm});
            skSolve(sketch);
        }
        {
            var Q0;
            {var subQ0=sQuery(id+"F4.wireOp",EDGE,"E11");var subQ1=sQuery(id+"F4.wireOp",EDGE,"E10");var subQ2=makeQuery(id+"F4.imprint","INTERSECT",VERTEX,{"derivedFrom":[subQ1,subQ0]});Q0=makeQuery(id+"F4.imprint","IMPRINT",FACE,{"disambiguationData":[TD([[makeQuery(id+"F4.imprint","IMPRINT",EDGE,{"disambiguationData":[TD([[subQ2,-1.0]])],"derivedFrom":subQ1}),-1.0]])]});}
            var Q1;
            {var subQ0=sQuery(id+"F4.wireOp",EDGE,"E11");var subQ1=sQuery(id+"F4.wireOp",EDGE,"E10");var subQ2=makeQuery(id+"F4.imprint","INTERSECT",VERTEX,{"derivedFrom":[subQ1,subQ0]});Q1=makeQuery(id+"F4.imprint","IMPRINT",FACE,{"disambiguationData":[TD([[makeQuery(id+"F4.imprint","IMPRINT",EDGE,{"disambiguationData":[TD([[subQ2,-1.0]])],"derivedFrom":subQ1}),1.0]])]});}
            var Q2;
            {var subQ0=sQuery(id+"F4.wireOp",EDGE,"E12");var subQ1=sQuery(id+"F4.wireOp",EDGE,"E10");var subQ2=makeQuery(id+"F4.imprint","INTERSECT",VERTEX,{"disambiguationData":[OD(0.0)],"derivedFrom":[subQ1,subQ0]});Q2=makeQuery(id+"F4.imprint","IMPRINT",FACE,{"disambiguationData":[TD([[makeQuery(id+"F4.imprint","IMPRINT",EDGE,{"disambiguationData":[TD([[subQ2,-1.0]])],"derivedFrom":subQ1}),1.0]])]});}
            var Q3;
            {var subQ0=sQuery(id+"F4.wireOp",EDGE,"E12");var subQ1=sQuery(id+"F4.wireOp",EDGE,"E10");var subQ2=makeQuery(id+"F4.imprint","INTERSECT",VERTEX,{"disambiguationData":[OD(0.0)],"derivedFrom":[subQ1,subQ0]});Q3=makeQuery(id+"F4.imprint","IMPRINT",FACE,{"disambiguationData":[TD([[makeQuery(id+"F4.imprint","IMPRINT",EDGE,{"disambiguationData":[TD([[subQ2,-1.0]])],"derivedFrom":subQ1}),-1.0]])]});}
            var Q4;
            {var subQ0=sQuery(id+"F4.wireOp",EDGE,"E10");var subQ1=sQuery(id+"F4.wireOp",EDGE,"E9");var subQ2=makeQuery(id+"F4.imprint","INTERSECT",VERTEX,{"disambiguationData":[OD(0.0)],"derivedFrom":[subQ1,subQ0]});Q4=makeQuery(id+"F4.imprint","IMPRINT",FACE,{"disambiguationData":[TD([[makeQuery(id+"F4.imprint","IMPRINT",EDGE,{"disambiguationData":[TD([[subQ2,1.0]])],"derivedFrom":subQ1}),1.0]])]});}
            var Q5;
            {var subQ0=sQuery(id+"F4.wireOp",EDGE,"E10");var subQ1=sQuery(id+"F4.wireOp",EDGE,"E9");var subQ2=makeQuery(id+"F4.imprint","INTERSECT",VERTEX,{"disambiguationData":[OD(1.0)],"derivedFrom":[subQ1,subQ0]});Q5=makeQuery(id+"F4.imprint","IMPRINT",FACE,{"disambiguationData":[TD([[makeQuery(id+"F4.imprint","IMPRINT",EDGE,{"disambiguationData":[TD([[subQ2,1.0]])],"derivedFrom":subQ1}),1.0]])]});}
            extrude(context, id + "F5", {"entities" : qUnion([Q0, Q1, Q2, Q3, Q4, Q5]), "operationType" : NewBodyOperationType.ADD, "depth" : 7.5 * mm, "offsetDistance" : 25 * mm});
        }
        {
            var Q0;
            {var subQ0=sQuery(id+"F4.wireOp",EDGE,"E10");var subQ1=sQuery(id+"F4.wireOp",EDGE,"E9");var subQ2=makeQuery(id+"F4.imprint","INTERSECT",VERTEX,{"disambiguationData":[OD(0.0)],"derivedFrom":[subQ1,subQ0]});Q0=makeQuery(id+"F4.imprint","IMPRINT",FACE,{"disambiguationData":[TD([[makeQuery(id+"F4.imprint","IMPRINT",EDGE,{"disambiguationData":[TD([[subQ2,-1.0]])],"derivedFrom":subQ1}),1.0]])]});}
            var Q1;
            {var subQ0=sQuery(id+"F4.wireOp",EDGE,"E10");var subQ1=sQuery(id+"F4.wireOp",EDGE,"E9");var subQ2=makeQuery(id+"F4.imprint","INTERSECT",VERTEX,{"disambiguationData":[OD(1.0)],"derivedFrom":[subQ1,subQ0]});Q1=makeQuery(id+"F4.imprint","IMPRINT",FACE,{"disambiguationData":[TD([[makeQuery(id+"F4.imprint","IMPRINT",EDGE,{"disambiguationData":[TD([[subQ2,-1.0]])],"derivedFrom":subQ1}),1.0]])]});}
            extrude(context, id + "F6", {"entities" : qUnion([Q0, Q1]), "operationType" : NewBodyOperationType.ADD, "depth" : 5 * mm, "offsetDistance" : 25 * mm});
        }
    });
